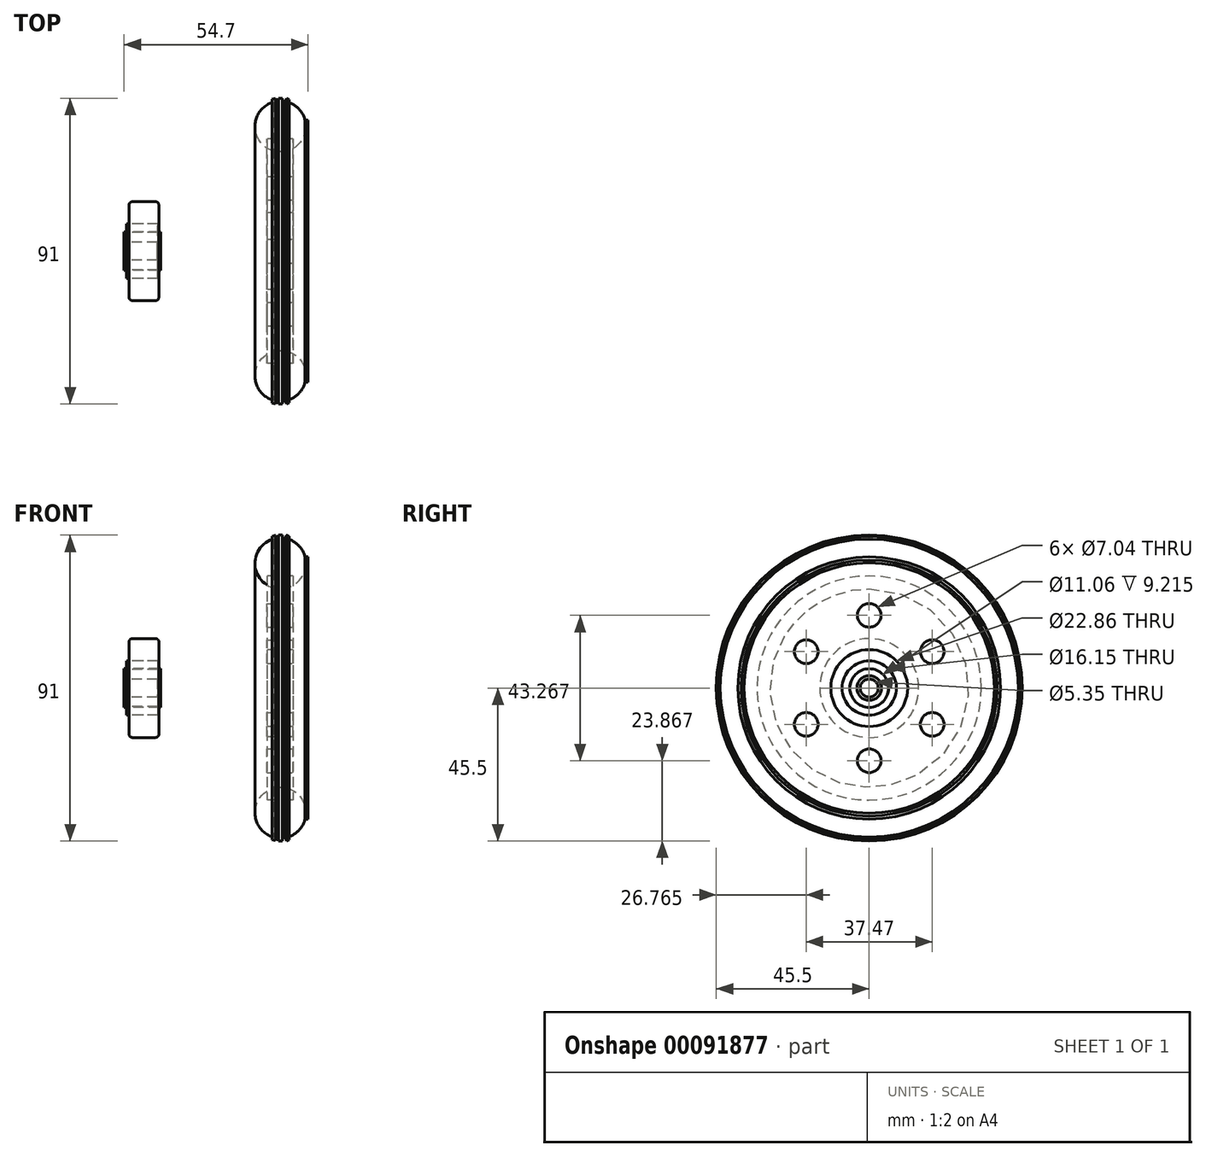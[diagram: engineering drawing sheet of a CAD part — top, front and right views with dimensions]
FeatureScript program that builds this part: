
annotation { "Feature Type Name" : "Feature", "Feature Type Description" : "" }
export const myFeature = defineFeature(function(context is Context, id is Id, definition is map)
    precondition{}
    {
        {
            var Q0;
            Q0=qCreatedBy(makeId("Front.planeOp"),FACE);
            var sketch = newSketch(context, id + "F0", { "sketchPlane" : qUnion([Q0])});
            skLineSegment(sketch, "E0", {"start": v(0, 0) * mm, "end": v(43.52, 0) * mm});
            skArc(sketch, "E1", {"start": v(-2.23, 44.34) * mm, "mid": v(-4.45, 30.97) * mm, "end": v(7.57, 37.23) * mm});
            skLineSegment(sketch, "E2", {"start": v(-0.57, 44.66) * mm, "end": v(-0.57, 45.5) * mm});
            skLineSegment(sketch, "E3", {"start": v(-0.57, 45.5) * mm, "end": v(0.6, 45.5) * mm});
            skLineSegment(sketch, "E4", {"start": v(0.6, 45.5) * mm, "end": v(0.6, 44.65) * mm});
            skLineSegment(sketch, "E5", {"start": v(0.6, 44.65) * mm, "end": v(1.4, 44.55) * mm});
            skLineSegment(sketch, "E6", {"start": v(1.4, 44.55) * mm, "end": v(1.78, 45.47) * mm});
            skLineSegment(sketch, "E7", {"start": v(1.78, 45.47) * mm, "end": v(2.6, 45.12) * mm});
            skLineSegment(sketch, "E8", {"start": v(2.6, 45.12) * mm, "end": v(2.27, 44.33) * mm});
            skLineSegment(sketch, "E9", {"start": v(-1.24, 44.58) * mm, "end": v(-1.46, 45.42) * mm});
            skLineSegment(sketch, "E10", {"start": v(-1.46, 45.42) * mm, "end": v(-2.45, 45.16) * mm});
            skLineSegment(sketch, "E11", {"start": v(-2.45, 45.16) * mm, "end": v(-2.23, 44.34) * mm});
            skArc(sketch, "E12.trimOffspring", {"start": v(-0.57, 44.66) * mm, "mid": v(-0.9, 44.62) * mm, "end": v(-1.24, 44.58) * mm});
            skArc(sketch, "E13.trimOffspring", {"start": v(1.4, 44.55) * mm, "mid": v(1, 44.61) * mm, "end": v(0.6, 44.65) * mm});
            skLineSegment(sketch, "E14", {"start": v(7.32, 39.03) * mm, "end": v(8.2, 39.03) * mm});
            skLineSegment(sketch, "E15", {"start": v(8.2, 39.03) * mm, "end": v(8.2, 38.09) * mm});
            skLineSegment(sketch, "E16", {"start": v(8.2, 38.09) * mm, "end": v(7.57, 37.23) * mm});
            skArc(sketch, "E17.trimOffspring", {"start": v(7.32, 39.03) * mm, "mid": v(5.48, 42.33) * mm, "end": v(2.27, 44.33) * mm});
            skSolve(sketch);
        }
        {
            var Q0;
            Q0=makeQuery(id+"F0.imprint","IMPRINT",FACE,{"disambiguationData":[TD([[makeQuery(id+"F0.imprint","IMPRINT",EDGE,{"derivedFrom":sQuery(id+"F0.wireOp",EDGE,"E1")}),1.0]])]});
            var Q1;
            Q1=sQuery(id+"F0.wireOp",EDGE,"E0");
            revolve(context, id + "F1", {"entities" : qUnion([Q0]), "axis" : qUnion([Q1]), "revolveType" : RevolveType.FULL});
        }
        {
            var Q0;
            Q0=qCreatedBy(makeId("Front.planeOp"),FACE);
            var sketch = newSketch(context, id + "F2", { "sketchPlane" : qUnion([Q0])});
            skLineSegment(sketch, "E18.bottom", {"start": v(-4.07, 33.35) * mm, "end": v(3.76, 33.35) * mm});
            skLineSegment(sketch, "E18.top", {"start": v(-4.07, 11.43) * mm, "end": v(3.76, 11.43) * mm});
            skLineSegment(sketch, "E18.left", {"start": v(-4.07, 33.35) * mm, "end": v(-4.07, 11.43) * mm});
            skLineSegment(sketch, "E18.right", {"start": v(3.76, 33.35) * mm, "end": v(3.76, 11.43) * mm});
            skSolve(sketch);
        }
        {
            var Q0;
            Q0 = qSketchRegion(id + "F2", true);
            var Q1;
            Q1=sQuery(id+"F0.wireOp",EDGE,"E0");
            revolve(context, id + "F3", {"entities" : qUnion([Q0]), "axis" : qUnion([Q1]), "revolveType" : RevolveType.FULL});
        }
        {
            var Q0;
            Q0=qCreatedBy(makeId("Right.planeOp"),FACE);
            var sketch = newSketch(context, id + "F4", { "sketchPlane" : qUnion([Q0])});
            skCircle(sketch, "E19", {"center": v(0, 21.63) * mm, "radius": 3.52 * mm});
            skCircle(sketch, "E20.1.0", {"center": v(-18.74, 10.82) * mm, "radius": 3.52 * mm});
            skCircle(sketch, "E20.2.0", {"center": v(-18.74, -10.82) * mm, "radius": 3.52 * mm});
            skPoint(sketch, "E20.center", {"position": v(0, 0) * mm});
            skCircle(sketch, "E21.1.3.0", {"center": v(0, -21.63) * mm, "radius": 3.52 * mm});
            skCircle(sketch, "E21.1.4.0", {"center": v(18.74, -10.82) * mm, "radius": 3.52 * mm});
            skCircle(sketch, "E21.1.5.0", {"center": v(18.74, 10.82) * mm, "radius": 3.52 * mm});
            skSolve(sketch);
        }
        {
            var Q0;
            Q0 = qSketchRegion(id + "F4", true);
            extrude(context, id + "F5", {"entities" : qUnion([Q0]), "operationType" : NewBodyOperationType.REMOVE, "oppositeDirection" : true, "depth" : 25 * mm, "symmetric" : true});
        }
        {
            var Q0;
            Q0=qCreatedBy(makeId("Front.planeOp"),FACE);
            var sketch = newSketch(context, id + "F6", { "sketchPlane" : qUnion([Q0])});
            skLineSegment(sketch, "E22.bottom", {"start": v(-44.04, 14.72) * mm, "end": v(-37.16, 14.72) * mm});
            skLineSegment(sketch, "E22.top", {"start": v(-45.04, 8.07) * mm, "end": v(-36.16, 8.07) * mm});
            skLineSegment(sketch, "E22.left", {"start": v(-45.04, 13.72) * mm, "end": v(-45.04, 8.07) * mm});
            skLineSegment(sketch, "E22.right", {"start": v(-36.16, 13.72) * mm, "end": v(-36.16, 8.07) * mm});
            skLineSegment(sketch, "E23.bottom", {"start": v(-36.16, 8.07) * mm, "end": v(-46.04, 8.07) * mm});
            skLineSegment(sketch, "E24", {"start": v(-46.23, -8.07) * mm, "end": v(-21.72, -8.07) * mm});
            skPoint(sketch, "E25.visualSharp", {"position": v(-45.04, 14.72) * mm});
            skArc(sketch, "E25.filletArc", {"start": v(-44.04, 14.72) * mm, "mid": v(-44.74, 14.43) * mm, "end": v(-45.04, 13.72) * mm});
            skPoint(sketch, "E26.visualSharp", {"position": v(-36.16, 14.72) * mm});
            skArc(sketch, "E26.filletArc", {"start": v(-36.16, 13.72) * mm, "mid": v(-36.45, 14.43) * mm, "end": v(-37.16, 14.72) * mm});
            skSolve(sketch);
        }
        {
            var Q0;
            Q0=makeQuery(id+"F6.imprint","IMPRINT",FACE,{"disambiguationData":[TD([[makeQuery(id+"F6.imprint","IMPRINT",EDGE,{"derivedFrom":sQuery(id+"F6.wireOp",EDGE,"E22.bottom")}),-1.0]])]});
            var Q1;
            Q1=sQuery(id+"F0.wireOp",EDGE,"E0");
            revolve(context, id + "F7", {"entities" : qUnion([Q0]), "axis" : qUnion([Q1]), "revolveType" : RevolveType.FULL});
        }
        {
            var Q0;
            Q0=makeQuery(id+"F6.imprint","IMPRINT",FACE,{"disambiguationData":[TD([[makeQuery(id+"F6.imprint","IMPRINT",EDGE,{"derivedFrom":sQuery(id+"F6.wireOp",EDGE,"E22.bottom")}),-1.0]])]});
            var sketch = newSketch(context, id + "F8", { "sketchPlane" : qUnion([Q0])});
            skLineSegment(sketch, "E27.bottom", {"start": v(-45.76, 8.07) * mm, "end": v(-36.54, 8.07) * mm});
            skLineSegment(sketch, "E27.top", {"start": v(-45.76, 5.53) * mm, "end": v(-36.54, 5.53) * mm});
            skLineSegment(sketch, "E27.left", {"start": v(-45.76, 8.07) * mm, "end": v(-45.76, 5.53) * mm});
            skLineSegment(sketch, "E27.right", {"start": v(-36.54, 8.07) * mm, "end": v(-36.54, 5.53) * mm});
            skSolve(sketch);
        }
        {
            var Q0;
            Q0 = qSketchRegion(id + "F8", true);
            var Q1;
            Q1=sQuery(id+"F0.wireOp",EDGE,"E0");
            revolve(context, id + "F9", {"entities" : qUnion([Q0]), "axis" : qUnion([Q1]), "revolveType" : RevolveType.FULL});
        }
        {
            var Q0;
            Q0=makeQuery(id+"F6.imprint","IMPRINT",FACE,{"disambiguationData":[TD([[makeQuery(id+"F6.imprint","IMPRINT",EDGE,{"derivedFrom":sQuery(id+"F6.wireOp",EDGE,"E22.bottom")}),-1.0]])]});
            var sketch = newSketch(context, id + "F10", { "sketchPlane" : qUnion([Q0])});
            skLineSegment(sketch, "E28.bottom", {"start": v(-46.5, 5.76) * mm, "end": v(-35.67, 5.76) * mm});
            skLineSegment(sketch, "E28.top", {"start": v(-45.5, 2.68) * mm, "end": v(-36.67, 2.68) * mm});
            skLineSegment(sketch, "E28.left", {"start": v(-46.5, 5.76) * mm, "end": v(-46.5, 3.68) * mm});
            skLineSegment(sketch, "E28.right", {"start": v(-35.67, 5.76) * mm, "end": v(-35.67, 3.68) * mm});
            skPoint(sketch, "E29.visualSharp", {"position": v(-46.5, 2.68) * mm});
            skPoint(sketch, "E30.visualSharp", {"position": v(-35.67, 2.68) * mm});
            skLineSegment(sketch, "E31", {"start": v(-46.5, 3.68) * mm, "end": v(-45.5, 2.68) * mm});
            skLineSegment(sketch, "E32", {"start": v(-35.67, 3.68) * mm, "end": v(-36.67, 2.68) * mm});
            skSolve(sketch);
        }
        {
            var Q0;
            Q0 = qSketchRegion(id + "F10", true);
            var Q1;
            Q1=sQuery(id+"F0.wireOp",EDGE,"E0");
            revolve(context, id + "F11", {"entities" : qUnion([Q0]), "axis" : qUnion([Q1]), "revolveType" : RevolveType.FULL});
        }
    });
